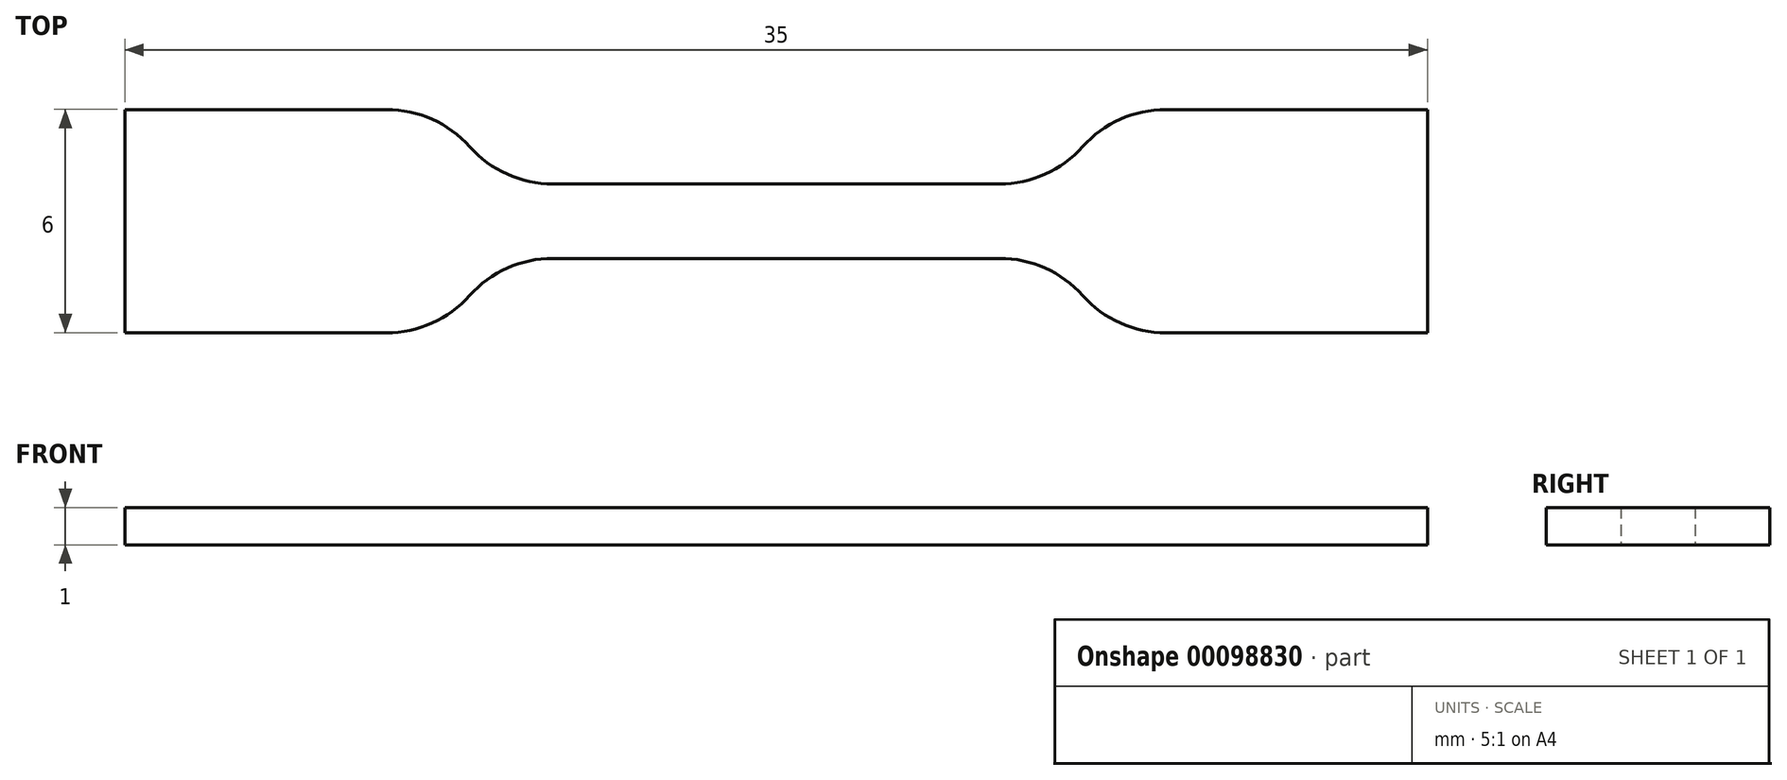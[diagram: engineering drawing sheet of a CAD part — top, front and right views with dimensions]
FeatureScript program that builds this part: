
annotation { "Feature Type Name" : "Feature", "Feature Type Description" : "" }
export const myFeature = defineFeature(function(context is Context, id is Id, definition is map)
    precondition{}
    {
        {
            var Q0;
            Q0=qCreatedBy(makeId("Top.planeOp"),FACE);
            var sketch = newSketch(context, id + "F0", { "sketchPlane" : qUnion([Q0])});
            skLineSegment(sketch, "E0", {"start": v(-17.5, 2.98) * mm, "end": v(-10.47, 2.98) * mm});
            skArc(sketch, "E1", {"start": v(-8.24, 1.98) * mm, "mid": v(-9.25, 2.71) * mm, "end": v(-10.47, 2.98) * mm});
            skArc(sketch, "E2", {"start": v(-8.24, 1.98) * mm, "mid": v(-7.22, 1.24) * mm, "end": v(-6, 0.98) * mm});
            skLineSegment(sketch, "E3", {"start": v(-6, 0.98) * mm, "end": v(0, 0.98) * mm});
            skLineSegment(sketch, "E4", {"start": v(-17.5, 2.98) * mm, "end": v(-17.5, -0.02) * mm});
            skLineSegment(sketch, "E5", {"start": v(0, 0.98) * mm, "end": v(0, -0.02) * mm});
            skLineSegment(sketch, "E6.MirrorCS", {"start": v(-17.5, -3.02) * mm, "end": v(-17.5, -0.02) * mm});
            skLineSegment(sketch, "E7.MirrorCS", {"start": v(-17.5, -3.02) * mm, "end": v(-10.47, -3.02) * mm});
            skArc(sketch, "E8.MirrorCS", {"start": v(-8.24, -2.02) * mm, "mid": v(-9.25, -2.76) * mm, "end": v(-10.47, -3.02) * mm});
            skArc(sketch, "E9.MirrorCS", {"start": v(-8.24, -2.02) * mm, "mid": v(-7.22, -1.29) * mm, "end": v(-6, -1.02) * mm});
            skLineSegment(sketch, "E10.MirrorCS", {"start": v(-6, -1.02) * mm, "end": v(0, -1.02) * mm});
            skLineSegment(sketch, "E11.MirrorCS", {"start": v(6, -1.02) * mm, "end": v(0, -1.02) * mm});
            skLineSegment(sketch, "E12.MirrorCS", {"start": v(6, 0.98) * mm, "end": v(0, 0.98) * mm});
            skArc(sketch, "E13.MirrorCS", {"start": v(8.24, 1.98) * mm, "mid": v(7.22, 1.24) * mm, "end": v(6, 0.98) * mm});
            skArc(sketch, "E14.MirrorCS", {"start": v(8.24, -2.02) * mm, "mid": v(7.22, -1.29) * mm, "end": v(6, -1.02) * mm});
            skArc(sketch, "E15.MirrorCS", {"start": v(8.24, -2.02) * mm, "mid": v(9.25, -2.76) * mm, "end": v(10.47, -3.02) * mm});
            skArc(sketch, "E16.MirrorCS", {"start": v(8.24, 1.98) * mm, "mid": v(9.25, 2.71) * mm, "end": v(10.47, 2.98) * mm});
            skLineSegment(sketch, "E17.MirrorCS", {"start": v(17.5, 2.98) * mm, "end": v(10.47, 2.98) * mm});
            skLineSegment(sketch, "E18.MirrorCS", {"start": v(17.5, -3.02) * mm, "end": v(10.47, -3.02) * mm});
            skLineSegment(sketch, "E19.MirrorCS", {"start": v(17.5, 2.98) * mm, "end": v(17.5, -0.02) * mm});
            skLineSegment(sketch, "E20.MirrorCS", {"start": v(17.5, -3.02) * mm, "end": v(17.5, -0.02) * mm});
            skSolve(sketch);
        }
        {
            var Q0;
            Q0=makeQuery(id+"F0.imprint","IMPRINT",FACE,{"disambiguationData":[TD([[makeQuery(id+"F0.imprint","IMPRINT",EDGE,{"derivedFrom":sQuery(id+"F0.wireOp",EDGE,"E0")}),-1.0]])]});
            var Q1;
            Q1=sQuery(id+"F0.wireOp",EDGE,"E0");
            var Q2;
            Q2=sQuery(id+"F0.wireOp",EDGE,"E1");
            var Q3;
            Q3=sQuery(id+"F0.wireOp",EDGE,"E2");
            var Q4;
            Q4=sQuery(id+"F0.wireOp",EDGE,"E3");
            var Q5;
            Q5=sQuery(id+"F0.wireOp",EDGE,"E4");
            var Q6;
            Q6=sQuery(id+"F0.wireOp",EDGE,"E5");
            var Q7;
            Q7=sQuery(id+"F0.wireOp",EDGE,"E6.MirrorCS");
            var Q8;
            Q8=sQuery(id+"F0.wireOp",EDGE,"E7.MirrorCS");
            var Q9;
            Q9=sQuery(id+"F0.wireOp",EDGE,"E8.MirrorCS");
            var Q10;
            Q10=sQuery(id+"F0.wireOp",EDGE,"E9.MirrorCS");
            var Q11;
            Q11=sQuery(id+"F0.wireOp",EDGE,"E10.MirrorCS");
            var Q12;
            Q12=sQuery(id+"F0.wireOp",EDGE,"E11.MirrorCS");
            var Q13;
            Q13=sQuery(id+"F0.wireOp",EDGE,"E12.MirrorCS");
            var Q14;
            Q14=sQuery(id+"F0.wireOp",EDGE,"E13.MirrorCS");
            var Q15;
            Q15=sQuery(id+"F0.wireOp",EDGE,"E14.MirrorCS");
            var Q16;
            Q16=sQuery(id+"F0.wireOp",EDGE,"E15.MirrorCS");
            var Q17;
            Q17=sQuery(id+"F0.wireOp",EDGE,"E16.MirrorCS");
            var Q18;
            Q18=sQuery(id+"F0.wireOp",EDGE,"E17.MirrorCS");
            var Q19;
            Q19=sQuery(id+"F0.wireOp",EDGE,"E18.MirrorCS");
            var Q20;
            Q20=sQuery(id+"F0.wireOp",EDGE,"E19.MirrorCS");
            var Q21;
            Q21=sQuery(id+"F0.wireOp",EDGE,"E20.MirrorCS");
            extrude(context, id + "F1", {"entities" : qUnion([Q0]), "surfaceEntities" : qUnion([Q1, Q2, Q3, Q4, Q5, Q6, Q7, Q8, Q9, Q10, Q11, Q12, Q13, Q14, Q15, Q16, Q17, Q18, Q19, Q20, Q21]), "depth" : 1 * mm});
        }
    });
